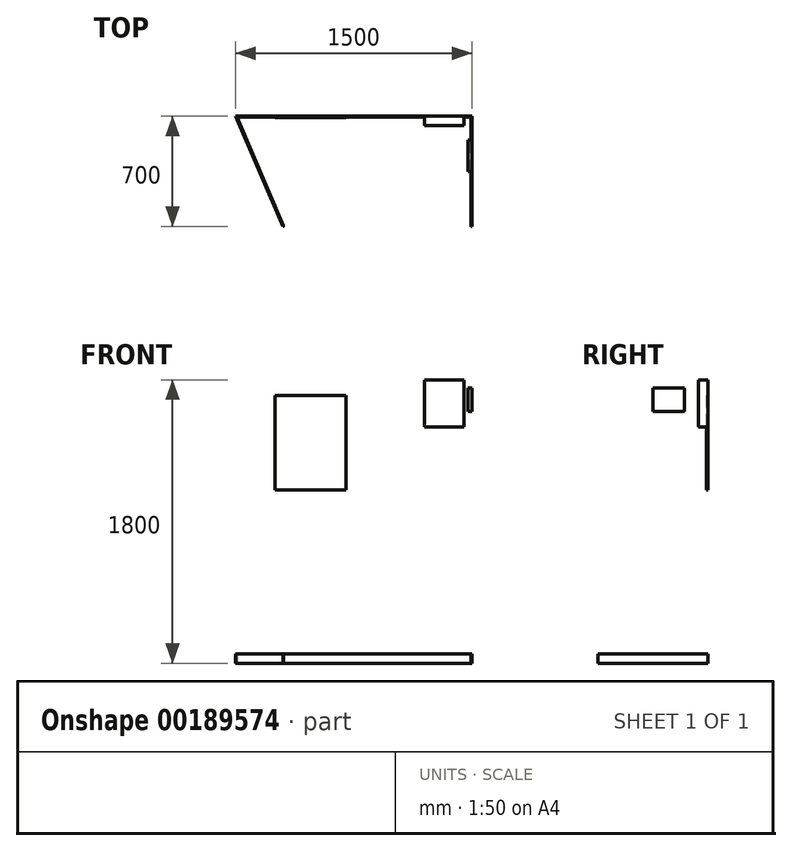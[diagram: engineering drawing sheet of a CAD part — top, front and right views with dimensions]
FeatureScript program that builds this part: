
annotation { "Feature Type Name" : "Feature", "Feature Type Description" : "" }
export const myFeature = defineFeature(function(context is Context, id is Id, definition is map)
    precondition{}
    {
        {
            var Q0;
            Q0=qCreatedBy(makeId("Top.planeOp"),FACE);
            var sketch = newSketch(context, id + "F0", { "sketchPlane" : qUnion([Q0])});
            skLineSegment(sketch, "E0.bottom", {"start": v(-68.17, 60.63) * mm, "end": v(1431.83, 60.63) * mm});
            skLineSegment(sketch, "E0.right", {"start": v(1431.83, 60.63) * mm, "end": v(1431.83, -639.37) * mm});
            skLineSegment(sketch, "E1", {"start": v(-68.17, 60.63) * mm, "end": v(231.83, -639.37) * mm});
            skLineSegment(sketch, "E2", {"start": v(1431.83, -639.37) * mm, "end": v(231.83, -639.37) * mm, "construction": true});
            skLineSegment(sketch, "E3.0", {"start": v(-60.59, 55.63) * mm, "end": v(236.43, -637.4) * mm});
            skLineSegment(sketch, "E4.0", {"start": v(1426.83, 55.63) * mm, "end": v(1426.83, -639.37) * mm});
            skLineSegment(sketch, "E5.trimOffspring", {"start": v(-60.59, 55.63) * mm, "end": v(1426.83, 55.63) * mm});
            skSolve(sketch);
        }
        {
            var Q0;
            Q0 = qSketchRegion(id + "F0", true);
            var Q1;
            Q1=sQuery(id+"F0.wireOp",EDGE,"E0.right");
            var Q2;
            Q2=sQuery(id+"F0.wireOp",EDGE,"E0.bottom");
            var Q3;
            Q3=sQuery(id+"F0.wireOp",EDGE,"E1");
            extrude(context, id + "F1", {"entities" : qUnion([Q0]), "bodyType" : ToolBodyType.SURFACE, "surfaceEntities" : qUnion([Q1, Q2, Q3]), "depth" : 2300 * mm});
        }
        {
            var Q0;
            Q0=sQuery(id+"F0.wireOp",EDGE,"E2");
            cPlane(context, id + "F2", {"entities" : qUnion([Q0]), "cplaneType" : CPlaneType.LINE_ANGLE, "offset" : 25 * mm, "angle" : 0 * degree, "width" : 150 * mm, "height" : 150 * mm});
        }
        {
            var Q0;
            Q0=qCreatedBy(id+"F2.planeOp",FACE);
            var sketch = newSketch(context, id + "F3", { "sketchPlane" : qUnion([Q0])});
            skLineSegment(sketch, "E6.bottom", {"start": v(1426.83, 0) * mm, "end": v(1431.83, 0) * mm});
            skLineSegment(sketch, "E6.top", {"start": v(1426.83, 60) * mm, "end": v(1431.83, 60) * mm});
            skLineSegment(sketch, "E6.left", {"start": v(1426.83, 0) * mm, "end": v(1426.83, 60) * mm});
            skLineSegment(sketch, "E6.right", {"start": v(1431.83, 0) * mm, "end": v(1431.83, 60) * mm});
            skSolve(sketch);
        }
        {
            var Q0;
            Q0 = qSketchRegion(id + "F3", true);
            var Q1;
            Q1=sQuery(id+"F0.wireOp",EDGE,"E3.0");
            var Q2;
            Q2=sQuery(id+"F0.wireOp",EDGE,"E5.trimOffspring");
            var Q3;
            Q3=sQuery(id+"F0.wireOp",EDGE,"E4.0");
            var Q4;
            Q4=sQuery(id+"F0.wireOp",EDGE,"E5.trimOffspring");
            var Q5;
            Q5=sQuery(id+"F0.wireOp",EDGE,"E3.0");
            sweep(context, id + "F4", {"profiles" : qUnion([Q0]), "surfaceProfiles" : qUnion([Q1, Q2]), "path" : qUnion([Q3, Q4, Q5])});
        }
        {
            var Q0;
            Q0=makeQuery(id+"F4.opSweep","SWEPT_EDGE",EDGE,{"disambiguationData":[OSD([sQuery(id+"F0.wireOp",EDGE,"E4.0"),sQuery(id+"F3.wireOp",EDGE,"E6.top"),sQuery(id+"F3.wireOp",EDGE,"E6.left")])]});
            var Q1;
            Q1=makeQuery(id+"F4.opSweep","SWEPT_EDGE",EDGE,{"disambiguationData":[OSD([sQuery(id+"F0.wireOp",EDGE,"E5.trimOffspring"),sQuery(id+"F3.wireOp",EDGE,"E6.top"),sQuery(id+"F3.wireOp",EDGE,"E6.left")])]});
            var Q2;
            Q2=makeQuery(id+"F4.opSweep","SWEPT_EDGE",EDGE,{"disambiguationData":[OSD([sQuery(id+"F0.wireOp",EDGE,"E3.0"),sQuery(id+"F3.wireOp",EDGE,"E6.top"),sQuery(id+"F3.wireOp",EDGE,"E6.left")])]});
            fillet(context, id + "F5", {"entities" : qUnion([Q0, Q1, Q2]), "radius" : 3 * mm, "tangentPropagation" : true, "allowEdgeOverflow" : false});
        }
        {
            var Q0;
            Q0=makeQuery(id+"F1.opExtrude","SWEPT_FACE",FACE,{"disambiguationData":[OSD([sQuery(id+"F0.wireOp",EDGE,"E0.bottom")])]});
            var sketch = newSketch(context, id + "F6", { "sketchPlane" : qUnion([Q0])});
            skLineSegment(sketch, "E7.bottom", {"start": v(1131.83, 1800) * mm, "end": v(1381.83, 1800) * mm});
            skLineSegment(sketch, "E7.top", {"start": v(1131.83, 1500) * mm, "end": v(1381.83, 1500) * mm});
            skLineSegment(sketch, "E7.left", {"start": v(1131.83, 1800) * mm, "end": v(1131.83, 1500) * mm});
            skLineSegment(sketch, "E7.right", {"start": v(1381.83, 1800) * mm, "end": v(1381.83, 1500) * mm});
            skSolve(sketch);
        }
        {
            var Q0;
            Q0=makeQuery(id+"F6.imprint","IMPRINT",FACE,{"disambiguationData":[TD([[makeQuery(id+"F6.imprint","IMPRINT",EDGE,{"derivedFrom":sQuery(id+"F6.wireOp",EDGE,"E7.bottom")}),-1.0]])]});
            extrude(context, id + "F7", {"entities" : qUnion([Q0]), "depth" : 60 * mm});
        }
        {
            var Q0;
            Q0=makeQuery(id+"F1.opExtrude","SWEPT_FACE",FACE,{"disambiguationData":[OSD([sQuery(id+"F0.wireOp",EDGE,"E0.right")])]});
            var sketch = newSketch(context, id + "F8", { "sketchPlane" : qUnion([Q0])});
            skLineSegment(sketch, "E8.bottom", {"start": v(89.37, 1750) * mm, "end": v(289.37, 1750) * mm});
            skLineSegment(sketch, "E8.top", {"start": v(89.37, 1600) * mm, "end": v(289.37, 1600) * mm});
            skLineSegment(sketch, "E8.left", {"start": v(89.37, 1750) * mm, "end": v(89.37, 1600) * mm});
            skLineSegment(sketch, "E8.right", {"start": v(289.37, 1750) * mm, "end": v(289.37, 1600) * mm});
            skSolve(sketch);
        }
        {
            var Q0;
            Q0=makeQuery(id+"F8.imprint","IMPRINT",FACE,{"disambiguationData":[TD([[makeQuery(id+"F8.imprint","IMPRINT",EDGE,{"derivedFrom":sQuery(id+"F8.wireOp",EDGE,"E8.bottom")}),-1.0]])]});
            extrude(context, id + "F9", {"entities" : qUnion([Q0]), "depth" : 25 * mm});
        }
        {
            var Q0;
            Q0=makeQuery(id+"F1.opExtrude","SWEPT_FACE",FACE,{"disambiguationData":[OSD([sQuery(id+"F0.wireOp",EDGE,"E0.bottom")])]});
            var sketch = newSketch(context, id + "F10", { "sketchPlane" : qUnion([Q0])});
            skLineSegment(sketch, "E9.bottom", {"start": v(181.83, 1700) * mm, "end": v(631.83, 1700) * mm});
            skLineSegment(sketch, "E9.top", {"start": v(181.83, 1100) * mm, "end": v(631.83, 1100) * mm});
            skLineSegment(sketch, "E9.left", {"start": v(181.83, 1700) * mm, "end": v(181.83, 1100) * mm});
            skLineSegment(sketch, "E9.right", {"start": v(631.83, 1700) * mm, "end": v(631.83, 1100) * mm});
            skSolve(sketch);
        }
        {
            var Q0;
            Q0 = qSketchRegion(id + "F10", true);
            extrude(context, id + "F11", {"entities" : qUnion([Q0]), "depth" : 10 * mm});
        }
    });
